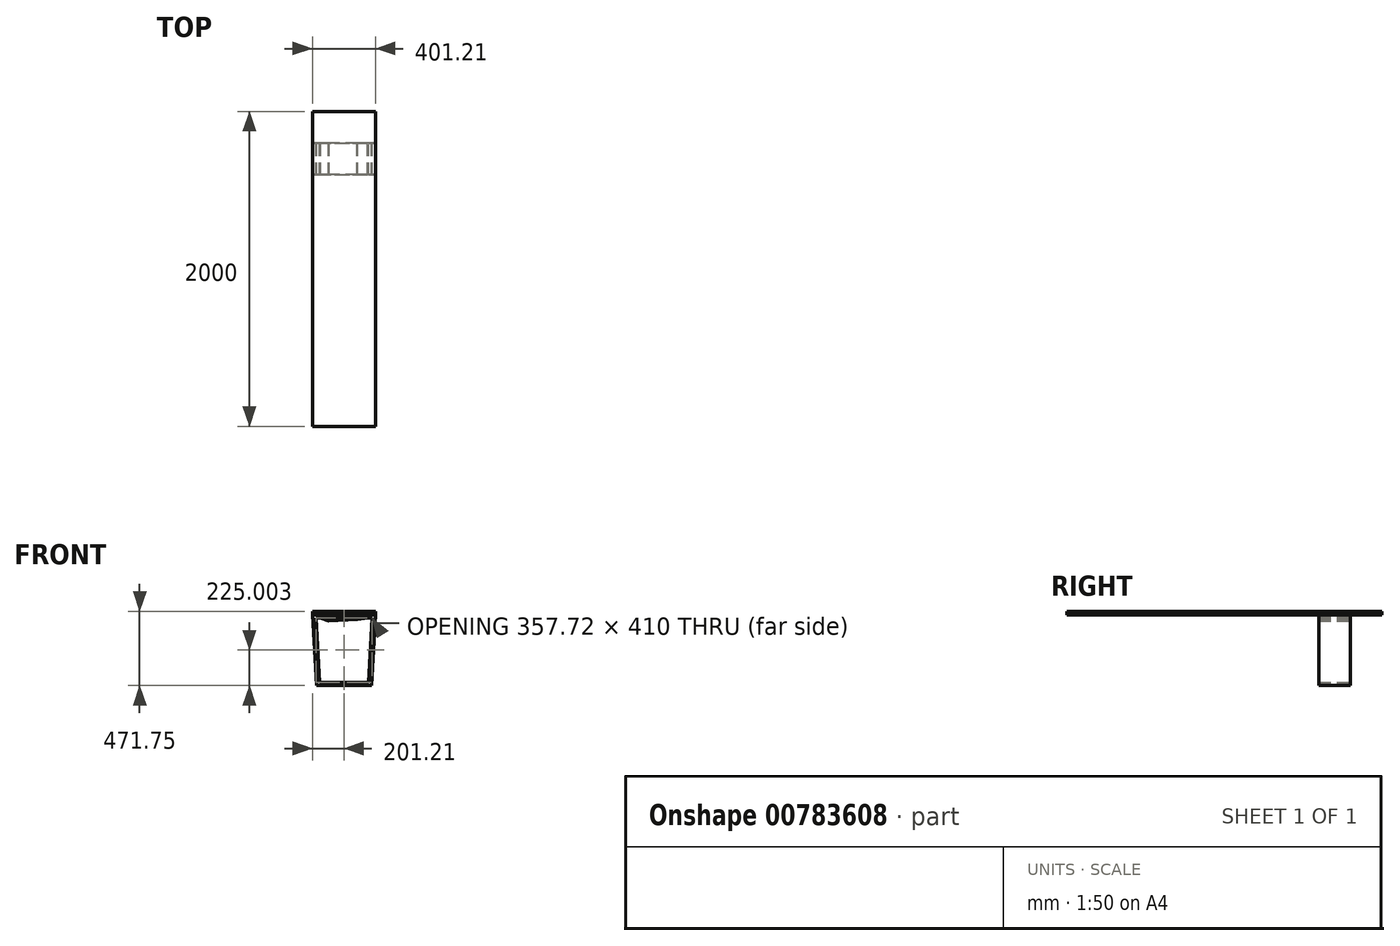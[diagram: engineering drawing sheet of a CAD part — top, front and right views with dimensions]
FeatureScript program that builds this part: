
annotation { "Feature Type Name" : "Feature", "Feature Type Description" : "" }
export const myFeature = defineFeature(function(context is Context, id is Id, definition is map)
    precondition{}
    {
        {
            var Q0;
            Q0=qCreatedBy(makeId("Front.planeOp"),FACE);
            var sketch = newSketch(context, id + "F0", { "sketchPlane" : qUnion([Q0])});
            skLineSegment(sketch, "E0", {"start": v(-200, 183.77) * mm, "end": v(-175, -266.23) * mm});
            skLineSegment(sketch, "E1", {"start": v(-175, -266.23) * mm, "end": v(175, -266.23) * mm});
            skLineSegment(sketch, "E2", {"start": v(175, -266.23) * mm, "end": v(200, 183.77) * mm});
            skLineSegment(sketch, "E3", {"start": v(200, 183.77) * mm, "end": v(150, 183.77) * mm});
            skLineSegment(sketch, "E4", {"start": v(150, 183.77) * mm, "end": v(84.28, 173.77) * mm});
            skLineSegment(sketch, "E5", {"start": v(84.28, 173.77) * mm, "end": v(-94.77, 163.77) * mm});
            skLineSegment(sketch, "E6", {"start": v(-94.77, 163.77) * mm, "end": v(-150, 183.77) * mm});
            skLineSegment(sketch, "E7", {"start": v(-150, 183.77) * mm, "end": v(-200, 183.77) * mm});
            skLineSegment(sketch, "E8.0", {"start": v(-178.86, 163.77) * mm, "end": v(-156.08, -246.23) * mm});
            skLineSegment(sketch, "E8.1", {"start": v(-153.5, 163.77) * mm, "end": v(-178.86, 163.77) * mm});
            skLineSegment(sketch, "E8.2", {"start": v(-156.08, -246.23) * mm, "end": v(156.08, -246.23) * mm});
            skLineSegment(sketch, "E8.3", {"start": v(-97.74, 143.58) * mm, "end": v(-153.5, 163.77) * mm});
            skLineSegment(sketch, "E8.4", {"start": v(156.08, -246.23) * mm, "end": v(178.86, 163.77) * mm});
            skLineSegment(sketch, "E8.5", {"start": v(178.86, 163.77) * mm, "end": v(151.51, 163.77) * mm});
            skLineSegment(sketch, "E8.6", {"start": v(151.51, 163.77) * mm, "end": v(86.34, 153.86) * mm});
            skLineSegment(sketch, "E8.7", {"start": v(86.34, 153.86) * mm, "end": v(-97.74, 143.58) * mm});
            skLineSegment(sketch, "E9", {"start": v(150, 183.77) * mm, "end": v(-150, 183.77) * mm});
            skLineSegment(sketch, "E10", {"start": v(-200, 183.77) * mm, "end": v(-201.21, 205.52) * mm});
            skLineSegment(sketch, "E11", {"start": v(-201.21, 205.52) * mm, "end": v(199.6, 205.52) * mm});
            skLineSegment(sketch, "E12", {"start": v(199.6, 205.52) * mm, "end": v(200, 183.77) * mm});
            skSolve(sketch);
        }
        {
            var Q0;
            Q0=makeQuery(id+"F0.imprint","IMPRINT",FACE,{"disambiguationData":[TD([[makeQuery(id+"F0.imprint","IMPRINT",EDGE,{"derivedFrom":sQuery(id+"F0.wireOp",EDGE,"E0")}),1.0]])]});
            extrude(context, id + "F1", {"entities" : qUnion([Q0]), "depth" : 200 * mm, "offsetDistance" : 25 * mm});
        }
        {
            var Q0;
            Q0=makeQuery(id+"F0.imprint","IMPRINT",FACE,{"disambiguationData":[TD([[makeQuery(id+"F0.imprint","IMPRINT",EDGE,{"derivedFrom":sQuery(id+"F0.wireOp",EDGE,"E3")}),-1.0]])]});
            extrude(context, id + "F2", {"entities" : qUnion([Q0]), "operationType" : NewBodyOperationType.ADD, "depth" : 1800 * mm, "offsetDistance" : 25 * mm});
        }
        {
            var Q0;
            Q0=makeQuery(id+"F0.imprint","IMPRINT",FACE,{"disambiguationData":[TD([[makeQuery(id+"F0.imprint","IMPRINT",EDGE,{"derivedFrom":sQuery(id+"F0.wireOp",EDGE,"E3")}),-1.0]])]});
            extrude(context, id + "F3", {"entities" : qUnion([Q0]), "operationType" : NewBodyOperationType.ADD, "oppositeDirection" : true, "depth" : 200 * mm, "offsetDistance" : 25 * mm});
        }
    });
